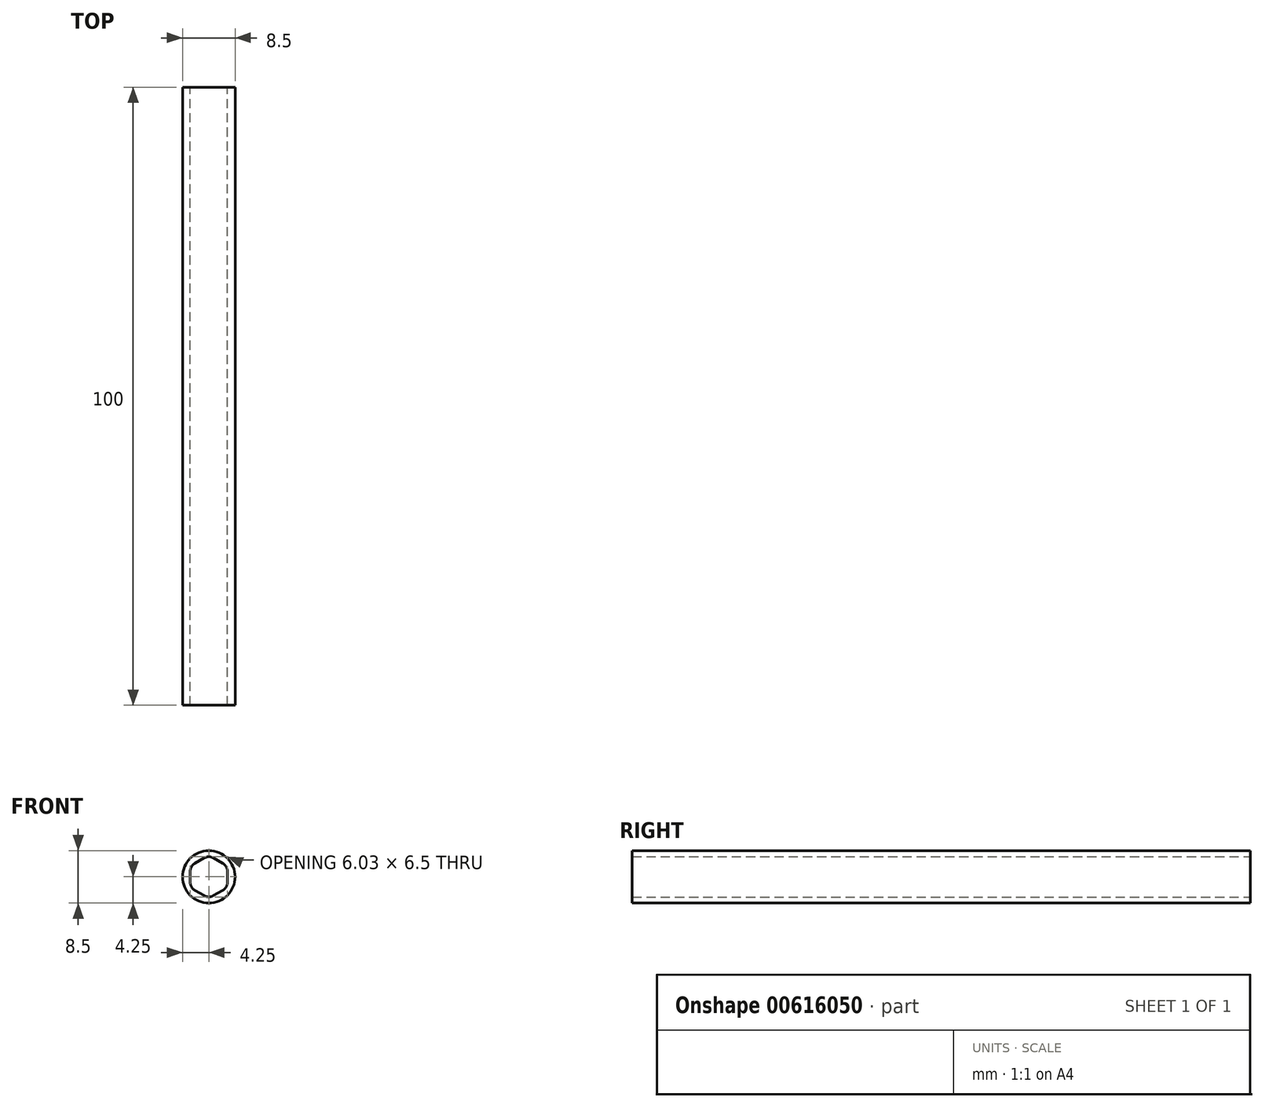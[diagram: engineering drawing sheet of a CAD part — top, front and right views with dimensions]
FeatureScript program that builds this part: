
annotation { "Feature Type Name" : "Feature", "Feature Type Description" : "" }
export const myFeature = defineFeature(function(context is Context, id is Id, definition is map)
    precondition{}
    {
        {
            var Q0;
            Q0=qCreatedBy(makeId("Front.planeOp"),FACE);
            var sketch = newSketch(context, id + "F0", { "sketchPlane" : qUnion([Q0])});
            skCircle(sketch, "E0.cCircle", {"center": v(0, 0) * mm, "radius": 3.02 * mm, "construction": true});
            skLineSegment(sketch, "E0.0", {"start": v(3.02, 0.87) * mm, "end": v(3.02, -0.87) * mm});
            skLineSegment(sketch, "E0.1", {"start": v(2.27, -2.17) * mm, "end": v(0.75, -3.05) * mm});
            skLineSegment(sketch, "E0.2", {"start": v(-0.75, -3.05) * mm, "end": v(-2.27, -2.17) * mm});
            skLineSegment(sketch, "E0.3", {"start": v(-3.02, -0.87) * mm, "end": v(-3.02, 0.87) * mm});
            skLineSegment(sketch, "E0.4", {"start": v(-2.27, 2.17) * mm, "end": v(-0.75, 3.05) * mm});
            skLineSegment(sketch, "E0.5", {"start": v(0.75, 3.05) * mm, "end": v(2.27, 2.17) * mm});
            skPoint(sketch, "E0.0.midPoint", {"position": v(3.02, 0) * mm});
            skPoint(sketch, "E1.visualSharp", {"position": v(0, 3.48) * mm});
            skArc(sketch, "E1.filletArc", {"start": v(0.75, 3.05) * mm, "mid": v(0, 3.25) * mm, "end": v(-0.75, 3.05) * mm});
            skPoint(sketch, "E2.visualSharp", {"position": v(3.02, 1.74) * mm});
            skArc(sketch, "E2.filletArc", {"start": v(3.02, 0.87) * mm, "mid": v(2.81, 1.62) * mm, "end": v(2.27, 2.17) * mm});
            skPoint(sketch, "E3.visualSharp", {"position": v(3.02, -1.74) * mm});
            skArc(sketch, "E3.filletArc", {"start": v(2.27, -2.17) * mm, "mid": v(2.81, -1.62) * mm, "end": v(3.02, -0.87) * mm});
            skPoint(sketch, "E4.visualSharp", {"position": v(0, -3.48) * mm});
            skArc(sketch, "E4.filletArc", {"start": v(-0.75, -3.05) * mm, "mid": v(0, -3.25) * mm, "end": v(0.75, -3.05) * mm});
            skPoint(sketch, "E5.visualSharp", {"position": v(-3.02, -1.74) * mm});
            skArc(sketch, "E5.filletArc", {"start": v(-3.02, -0.87) * mm, "mid": v(-2.81, -1.62) * mm, "end": v(-2.27, -2.17) * mm});
            skPoint(sketch, "E6.visualSharp", {"position": v(-3.02, 1.74) * mm});
            skArc(sketch, "E6.filletArc", {"start": v(-2.27, 2.17) * mm, "mid": v(-2.81, 1.62) * mm, "end": v(-3.02, 0.87) * mm});
            skCircle(sketch, "E7", {"center": v(0, 0) * mm, "radius": 4.25 * mm});
            skSolve(sketch);
        }
        {
            var Q0;
            Q0=makeQuery(id+"F0.imprint","IMPRINT",FACE,{"disambiguationData":[TD([[makeQuery(id+"F0.imprint","IMPRINT",EDGE,{"derivedFrom":sQuery(id+"F0.wireOp",EDGE,"E0.0")}),1.0]])]});
            extrude(context, id + "F1", {"entities" : qUnion([Q0]), "depth" : 100 * mm, "offsetDistance" : 25 * mm});
        }
        {
            var Q0;
            Q0=qCreatedBy(makeId("Front.planeOp"),FACE);
            cPlane(context, id + "F2", {"entities" : qUnion([Q0]), "cplaneType" : CPlaneType.OFFSET, "offset" : 3 * mm, "width" : 150 * mm, "height" : 150 * mm});
        }
        {
            var Q0;
            Q0=qCreatedBy(id+"F2.planeOp",FACE);
            var sketch = newSketch(context, id + "F3", { "sketchPlane" : qUnion([Q0])});
            skCircle(sketch, "E8", {"center": v(0, 0) * mm, "radius": 4.25 * mm});
            skArc(sketch, "E9", {"start": v(2.27, 2.17) * mm, "mid": v(2.81, 1.62) * mm, "end": v(3.02, 0.87) * mm});
            skLineSegment(sketch, "E10", {"start": v(3.02, -0.87) * mm, "end": v(3.02, 0.87) * mm});
            skArc(sketch, "E11", {"start": v(3.02, -0.87) * mm, "mid": v(2.81, -1.62) * mm, "end": v(2.27, -2.17) * mm});
            skLineSegment(sketch, "E12", {"start": v(0.75, -3.05) * mm, "end": v(2.27, -2.17) * mm});
            skArc(sketch, "E13", {"start": v(0.75, -3.05) * mm, "mid": v(0, -3.25) * mm, "end": v(-0.75, -3.05) * mm});
            skLineSegment(sketch, "E14", {"start": v(-2.27, -2.17) * mm, "end": v(-0.75, -3.05) * mm});
            skArc(sketch, "E15", {"start": v(-2.27, -2.17) * mm, "mid": v(-2.81, -1.62) * mm, "end": v(-3.02, -0.87) * mm});
            skLineSegment(sketch, "E16", {"start": v(-3.02, 0.87) * mm, "end": v(-3.02, -0.87) * mm});
            skArc(sketch, "E17", {"start": v(-3.02, 0.87) * mm, "mid": v(-2.81, 1.62) * mm, "end": v(-2.27, 2.17) * mm});
            skLineSegment(sketch, "E18", {"start": v(-0.75, 3.05) * mm, "end": v(-2.27, 2.17) * mm});
            skArc(sketch, "E19", {"start": v(-0.75, 3.05) * mm, "mid": v(0, 3.25) * mm, "end": v(0.75, 3.05) * mm});
            skLineSegment(sketch, "E20", {"start": v(2.27, 2.17) * mm, "end": v(0.75, 3.05) * mm});
            skArc(sketch, "E21", {"start": v(0, 2.92) * mm, "mid": v(0, 2.92) * mm, "end": v(0, 2.92) * mm});
            skPoint(sketch, "E21.first.point", {"position": v(-1.85, -2.41) * mm});
            skPoint(sketch, "E21.second.point", {"position": v(1.84, -2.42) * mm});
            skPoint(sketch, "E21.third.point", {"position": v(0, 2.92) * mm});
            skLineSegment(sketch, "E22", {"start": v(0, 3.25) * mm, "end": v(0, -4.25) * mm});
            skSolve(sketch);
        }
        {
            var Q0;
            {var subQ0=sQuery(id+"F3.wireOp",EDGE,"E21");var subQ1=sQuery(id+"F3.wireOp",EDGE,"E12");var subQ2=makeQuery(id+"F3.imprint","INTERSECT",VERTEX,{"disambiguationData":[OD(0.0)],"derivedFrom":[subQ1,subQ0]});Q0=makeQuery(id+"F3.imprint","IMPRINT",FACE,{"disambiguationData":[TD([[makeQuery(id+"F3.imprint","IMPRINT",EDGE,{"disambiguationData":[TD([[subQ2,-1.0]])],"derivedFrom":subQ1}),1.0]])]});}
            var Q1;
            Q1=sQuery(id+"F3.wireOp",EDGE,"E22");
            revolve(context, id + "F4", {"surfaceOperationType" : NewSurfaceOperationType.NEW, "entities" : qUnion([Q0]), "axis" : qUnion([Q1]), "revolveType" : RevolveType.FULL});
        }
        {
            var Q0;
            Q0=makeQuery(id+"F4.opRevolve","SWEPT_BODY",BODY,{"disambiguationData":[OSD([sQuery(id+"F3.wireOp",EDGE,"E9"),sQuery(id+"F3.wireOp",EDGE,"E10"),sQuery(id+"F3.wireOp",EDGE,"E11"),sQuery(id+"F3.wireOp",EDGE,"E12"),sQuery(id+"F3.wireOp",EDGE,"E13"),sQuery(id+"F3.wireOp",EDGE,"E19"),sQuery(id+"F3.wireOp",EDGE,"E20"),sQuery(id+"F3.wireOp",EDGE,"E22")])]});
            deleteBodies(context, id + "F5", {"entities" : qUnion([Q0])});
        }
    });
